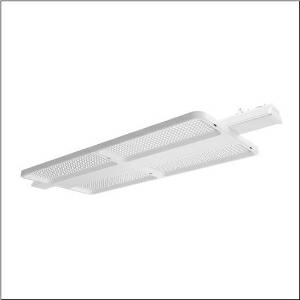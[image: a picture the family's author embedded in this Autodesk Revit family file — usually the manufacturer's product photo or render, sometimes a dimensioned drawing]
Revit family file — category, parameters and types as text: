
# Revit family: highbay_11_fur_licross_r__tragschiene_maxi_51hn12db4rla02_6f6b
name_source: partatom
category: Lighting Fixtures
units: mm (PartAtom-declared; Revit-internal decimal feet)

## family parameters
Cut with Voids When Loaded = No
Host = Face
Light Source = No
Part Type = Normal
Room Calculation Point = No
Round Connector Dimension = Use Diameter
Shared = No

## types (1)
- --- (1 x LED, 42500 lm, 214.2 W, 4000K)
    Apparent Load = 214 VA
    CIE Flux Codes = 87 98 100 100 100
    Color Rendering = 80
    Color Temperature = 4000K
    Default Elevation = 1800 mm
    Description = high bay luminaire Highbay 11 for Licross® trunking rail maxi; direct symmetric wide distribution, light control with lens of PMMA; UGR ≤ 22 (X = 4H | Y = 8H | S = 0.25H | reflection values 70/50/20); luminous flux: 42.500lm; light colour: 840, colour temperature: 4000K, MacAdam ≤ 2 SDCM (initial), colour rendering: CRI > 80; luminous efficacy: 198,4lm/W; rated service life: 100.000h (L95/B50) at AT= 25°C; control: Bluetooth® Mesh; for wireless networking: Node luminaire for setting up a local control solution without a higher-level application controller, intelligence completely in the luminaire; no control line such as DALI between the Node multi-sensor luminaires and Nodes is required, wireless integration of other Node luminaires and Node multi-sensor luminaires into the network is possible; number of Node luminaires in the project can be expanded as required, network sizes > 300 Nodes can be realized; can also be connected to lighting or building automation via various gateways upon request; integrated DALI2 ECG provides luminaire data (according to IEC62386, Part 251), energy data (Part 252), and monitoring and analytics data (Part 253) to higher-level systems for further processing; luminaire connection: plug, 5-pole, with phase selectionmains connection: 230..240V, AC 50/60Hz; connected load: 214,2W; protection rating (complete): IP64; insulation class (complete): insulation class I (protective earthing); protection symbol: D; impact resistance: IK07; certification: CE, ENEC, VDE, UKCA; internal wiring halogen-free; luminaire corresponds to IFS (International Featured Standards) requirements for safety and quality in the food industry; LABS conformity tested according to VDMA 24364:2018-05; housing frame of high-performance plastic PA6, matt traffic white (RAL 9016); cover of PMMA; fixing on rail side of steel, galvanised, white; blank cover of PC/ABS, traffic white (RAL 9016); dimension (LxWxH): 1.250 x 442 x 72mm; permissible operating ambient temperature: -20..+35°C (reducing of maximum allowable ambient temperature of 5°C with ceiling mounting); packaging unit: 1 piece
    Height = 72 mm  [stored 0.23622 ft]
    Lamp = 1 x LED
    Lamp Light Flux = 42500 lm
    Lamp Power = 214.2 W
    Lamp count = 1
    Length = 946 mm
    Luminous efficacy = 198 lm/W
    Manufacturer = Siteco
    ModVariant = No
    Model = 51HN12DB4RLA02
    Mounting Place = Ceiling
    Mounting Type = Pendant
    Number of Poles = 1
    OnlyDefault = Yes
    Power Factor = 1
    Product Name = Highbay 11 für Licross® Tragschiene maxi
    Product group = high bay luminaire
    ProductGroupID = 901
    Protection Class = Protection class I
    Protection Degree = IP 64
    RLX_Detail_Level = 1
    RLX_Emergency_Light_Flux = 0 lm
    RLX_Emergency_Type = 0
    RLX_Emergency_Type_DB = No
    RlxData = <blob elided: 25189 chars, md5=fc6f0be1>
    Socket = socket
    Standby Power = 0 W
    System Light Flux = 42499 lm
    System Power = 214 W
    Type Comments = factory setting: luminous flux: 100 % | dim-lin: 254 | 983 mA
    Type Image = l_1361711.jpg
    URL = http://relux.com
    VarID = @adj_013519
    Voltage = 0 V
    Weight = 0.00 kg
    Width = 442 mm

note: [stored X ft] marks values corroborated as IEEE doubles in the binary element streams (Revit-internal decimal feet)

## geometry (parser evidence)
native form markers: Blend x4, Sweep x10
no freeform markers — native parametric forms only
